# Revit family: WL-RxX145-xxx-Px
name_source: partatom
category: Leuchten
revit_build: Autodesk Revit 2017 (Build: 20190508_0315(x64)
units: mm (PartAtom-declared; Revit-internal decimal feet)

## family parameters
Basisbauteil = Fläche
Beim Laden mit Abzugskörper schneiden = Nein
Bemaßung runder Anschluss = Durchmesser verwenden
Gemeinsam genutzt = Nein
Lichtquelle = Ja
OmniClass-Nummer = 23.80.70.11
OmniClass-Titel = Luminaries for Internal Lighting
Raumberechnungspunkt = Nein
Teiletyp = Normal

## types (7) — shared parameters
Baugruppenkennzeichen = D5020200
Emissionsform beim Rendern sichtbar = Nein
Farbfilter = 16777215
Farbtemperaturverschiebung bei Dämpfen der Lampe = <Keine Auswahl>
Hersteller = RIDI Leuchten GmbH
Lampe = LED
Neigungswinkel = 90.00°
URL = www.ridi.de
Von Breite des Rechtecks ausssenden = 1464 mm
Von Länge des Rechtecks aussenden = 178 mm  [stored 0.58399 ft]
brand = RIDI
conformity mark = CE
electrical safety class = 1
height = 60 mm  [stored 0.19685 ft]
ingress protection (IP) code = IP40
length = 1520 mm
nominal frequency = 50-60Hz
nominal voltage = 230
voltage type (AC, DC, UC) = AC
weight = 3,26kg
width = 178 mm  [stored 0.58399 ft]
zero-valued in all types: Vorgabe-Ansicht

## per-type parameters (varying)
| type | Datei für fotometrisches Netz | Modell | Scheinlast | rated input power |
| WL-R2X145/35ND-P | WL-R2x14535ND-P-450M840.IES | 0450033 | 62 VA | 62 |
| WL-R2X145/35DA-P | WL-R2x14535ND-P-450M840.IES | 0460033 | 62 VA | 62 |
| WL-R2X145/35ND-P-SET | WL-R2x14535ND-P-450M840.IES | 0450033//676 | 62 VA | 62 |
| WL-R1X145/45ND-P | WL-R1x14545ND-P-450M840.IES | 0450071 | 49 VA | 49 |
| WL-R1X145/45DA-P | WL-R1x14545ND-P-450M840.IES | 0460071 | 49 VA | 49 |
| WL-R1X145/45ND-P-SET | WL-R1x14545ND-P-450M840.IES | 0450071//676 | 49 VA | 49 |
| WL-R1X145/35ND-P-SET | WL-R1x14545ND-P-450M840.IES | 0450005//676 | 31 VA | 31 |

note: column(s) folded — value = type name in every type: product name

note: [stored X ft] marks values corroborated as IEEE doubles in the binary element streams (Revit-internal decimal feet)
